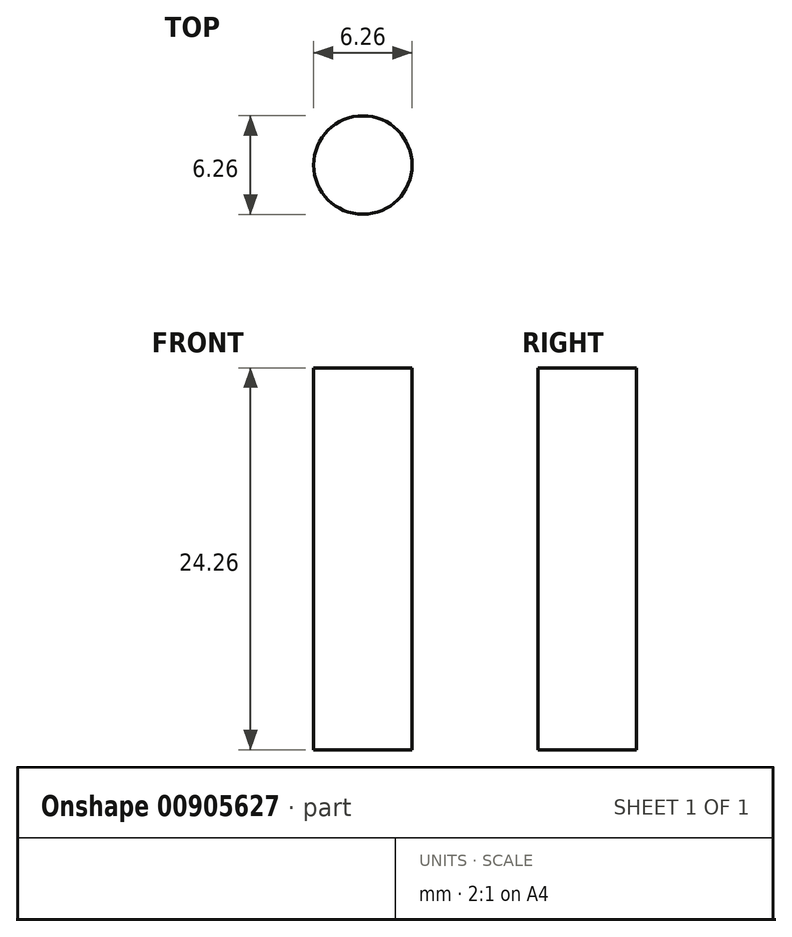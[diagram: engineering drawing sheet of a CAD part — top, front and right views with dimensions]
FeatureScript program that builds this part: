
annotation { "Feature Type Name" : "Feature", "Feature Type Description" : "" }
export const myFeature = defineFeature(function(context is Context, id is Id, definition is map)
    precondition{}
    {
        {
            var Q0;
            Q0=qCreatedBy(makeId("Top.planeOp"),FACE);
            var sketch = newSketch(context, id + "F0", { "sketchPlane" : qUnion([Q0])});
            skCircle(sketch, "E0", {"center": v(0, 0) * mm, "radius": 3.12 * mm});
            skSolve(sketch);
        }
        {
            var Q0;
            Q0 = qSketchRegion(id + "F0", true);
            extrude(context, id + "F1", {"entities" : qUnion([Q0]), "endBound" : BoundingType.SYMMETRIC, "depth" : 24.25 * mm, "offsetDistance" : 25 * mm});
        }
    });
